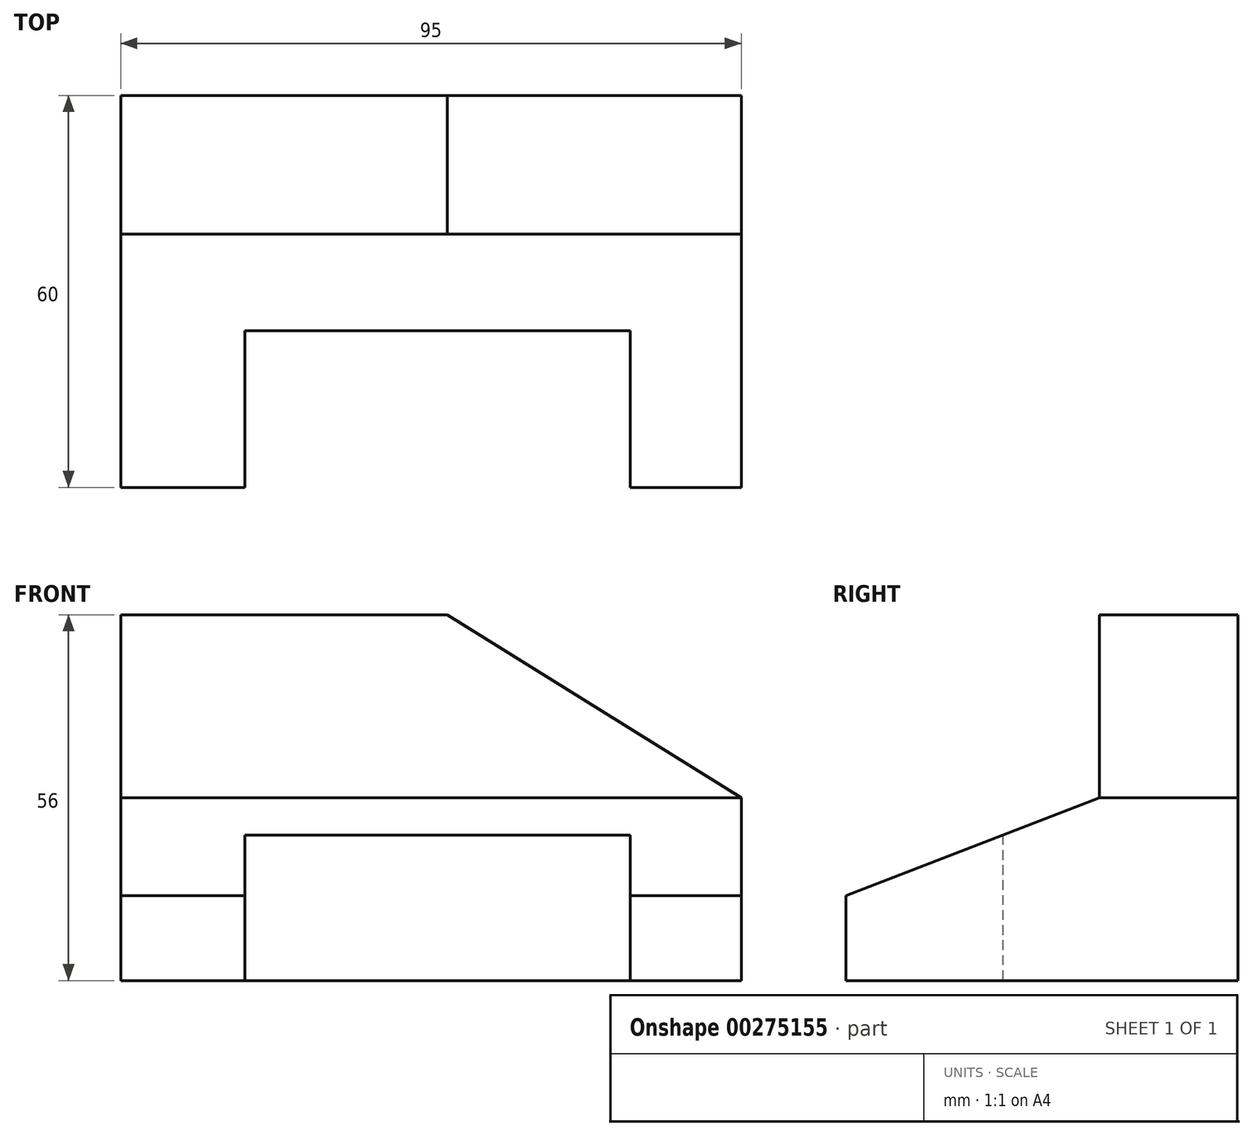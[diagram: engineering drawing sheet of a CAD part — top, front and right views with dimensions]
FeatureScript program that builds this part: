
annotation { "Feature Type Name" : "Feature", "Feature Type Description" : "" }
export const myFeature = defineFeature(function(context is Context, id is Id, definition is map)
    precondition{}
    {
        {
            var Q0;
            Q0=qCreatedBy(makeId("Right.planeOp"),FACE);
            var sketch = newSketch(context, id + "F0", { "sketchPlane" : qUnion([Q0])});
            skLineSegment(sketch, "E0", {"start": v(0, 0) * mm, "end": v(0, 56) * mm});
            skLineSegment(sketch, "E1", {"start": v(0, 56) * mm, "end": v(-21.2, 56) * mm});
            skLineSegment(sketch, "E2", {"start": v(-21.2, 56) * mm, "end": v(-21.2, 28) * mm});
            skLineSegment(sketch, "E3", {"start": v(-21.2, 28) * mm, "end": v(-60, 13) * mm});
            skLineSegment(sketch, "E4", {"start": v(-60, 13) * mm, "end": v(-60, 0) * mm});
            skLineSegment(sketch, "E5", {"start": v(-60, 0) * mm, "end": v(0, 0) * mm});
            skSolve(sketch);
        }
        {
            var Q0;
            Q0 = qSketchRegion(id + "F0", true);
            extrude(context, id + "F1", {"entities" : qUnion([Q0]), "oppositeDirection" : true, "depth" : 95 * mm});
        }
        {
            var Q0;
            Q0=makeQuery(id+"F1.opExtrude","SWEPT_FACE",FACE,{"disambiguationData":[OSD([sQuery(id+"F0.wireOp",EDGE,"E2")])]});
            var sketch = newSketch(context, id + "F2", { "sketchPlane" : qUnion([Q0])});
            skLineSegment(sketch, "E6", {"start": v(-38.89, 56) * mm, "end": v(0, 28) * mm});
            skSolve(sketch);
        }
        {
            var Q0;
            {var subQ0=sQuery(id+"F2.wireOp",EDGE,"E6");Q0=makeQuery(id+"F2.imprint","IMPRINT",FACE,{"disambiguationData":[TD([[makeQuery(id+"F2.imprint","IMPRINT",EDGE,{"derivedFrom":subQ0}),1.0]])]});}
            var Q1;
            Q1=qCreatedBy(makeId("Front.planeOp"),FACE);
            extrude(context, id + "F3", {"entities" : qUnion([Q0]), "operationType" : NewBodyOperationType.ADD, "endBound" : BoundingType.UP_TO_SURFACE, "oppositeDirection" : true, "endBoundEntityFace" : qUnion([Q1]), "depth" : 25 * mm});
        }
        {
            var Q0;
            Q0=makeQuery(id+"F1.opExtrude","SWEPT_FACE",FACE,{"disambiguationData":[OSD([sQuery(id+"F0.wireOp",EDGE,"E2")])]});
            var sketch = newSketch(context, id + "F4", { "sketchPlane" : qUnion([Q0])});
            skLineSegment(sketch, "E7", {"start": v(-45, 56) * mm, "end": v(0, 28) * mm});
            skSolve(sketch);
        }
        {
            var Q0;
            {var subQ0=sQuery(id+"F4.wireOp",EDGE,"E7");Q0=makeQuery(id+"F4.imprint","IMPRINT",FACE,{"disambiguationData":[TD([[makeQuery(id+"F4.imprint","IMPRINT",EDGE,{"derivedFrom":subQ0}),1.0]])]});}
            extrude(context, id + "F5", {"entities" : qUnion([Q0]), "operationType" : NewBodyOperationType.REMOVE, "oppositeDirection" : true, "depth" : 25 * mm});
        }
        {
            var Q0;
            Q0=makeQuery(id+"F1.opExtrude","SWEPT_FACE",FACE,{"disambiguationData":[OSD([sQuery(id+"F0.wireOp",EDGE,"E5")])]});
            var sketch = newSketch(context, id + "F6", { "sketchPlane" : qUnion([Q0])});
            skLineSegment(sketch, "E8.bottom", {"start": v(-76, 60) * mm, "end": v(-17, 60) * mm});
            skLineSegment(sketch, "E8.top", {"start": v(-76, 36) * mm, "end": v(-17, 36) * mm});
            skLineSegment(sketch, "E8.left", {"start": v(-76, 60) * mm, "end": v(-76, 36) * mm});
            skLineSegment(sketch, "E8.right", {"start": v(-17, 60) * mm, "end": v(-17, 36) * mm});
            skSolve(sketch);
        }
        {
            var Q0;
            Q0=makeQuery(id+"F6.imprint","IMPRINT",FACE,{"disambiguationData":[TD([[makeQuery(id+"F6.imprint","IMPRINT",EDGE,{"derivedFrom":sQuery(id+"F6.wireOp",EDGE,"E8.bottom")}),-1.0]])]});
            extrude(context, id + "F7", {"entities" : qUnion([Q0]), "operationType" : NewBodyOperationType.REMOVE, "oppositeDirection" : true, "depth" : 30 * mm});
        }
        {
            var Q0;
            Q0=makeQuery(id+"F1.opExtrude","SWEPT_BODY",BODY,{"disambiguationData":[OSD([sQuery(id+"F0.wireOp",EDGE,"E0"),sQuery(id+"F0.wireOp",EDGE,"E1"),sQuery(id+"F0.wireOp",EDGE,"E2"),sQuery(id+"F0.wireOp",EDGE,"E3"),sQuery(id+"F0.wireOp",EDGE,"E4"),sQuery(id+"F0.wireOp",EDGE,"E5")])]});
            var Q1;
            Q1=makeQuery(id+"F1.opExtrude","SWEPT_EDGE",EDGE,{"disambiguationData":[OSD([sQuery(id+"F0.wireOp",EDGE,"E0"),sQuery(id+"F0.wireOp",EDGE,"E5")])]});
            var Q2;
            Q2=makeQuery(id+"F7.boolean.opBoolean","INTERSECT",EDGE,{"derivedFrom":[makeQuery(id+"F1.opExtrude","SWEPT_FACE",FACE,{"disambiguationData":[OSD([sQuery(id+"F0.wireOp",EDGE,"E3")])]}),makeQuery(id+"F7.opExtrude","SWEPT_FACE",FACE,{"disambiguationData":[OSD([sQuery(id+"F6.wireOp",EDGE,"E8.top")])]})]});
            transform(context, id + "F8", {"entities" : qUnion([Q0]), "transformType" : TransformType.TRANSLATION_ENTITY, "oppositeDirectionEntity" : false, "transformLine" : qUnion([Q1]), "makeCopy" : false});
        }
    });
